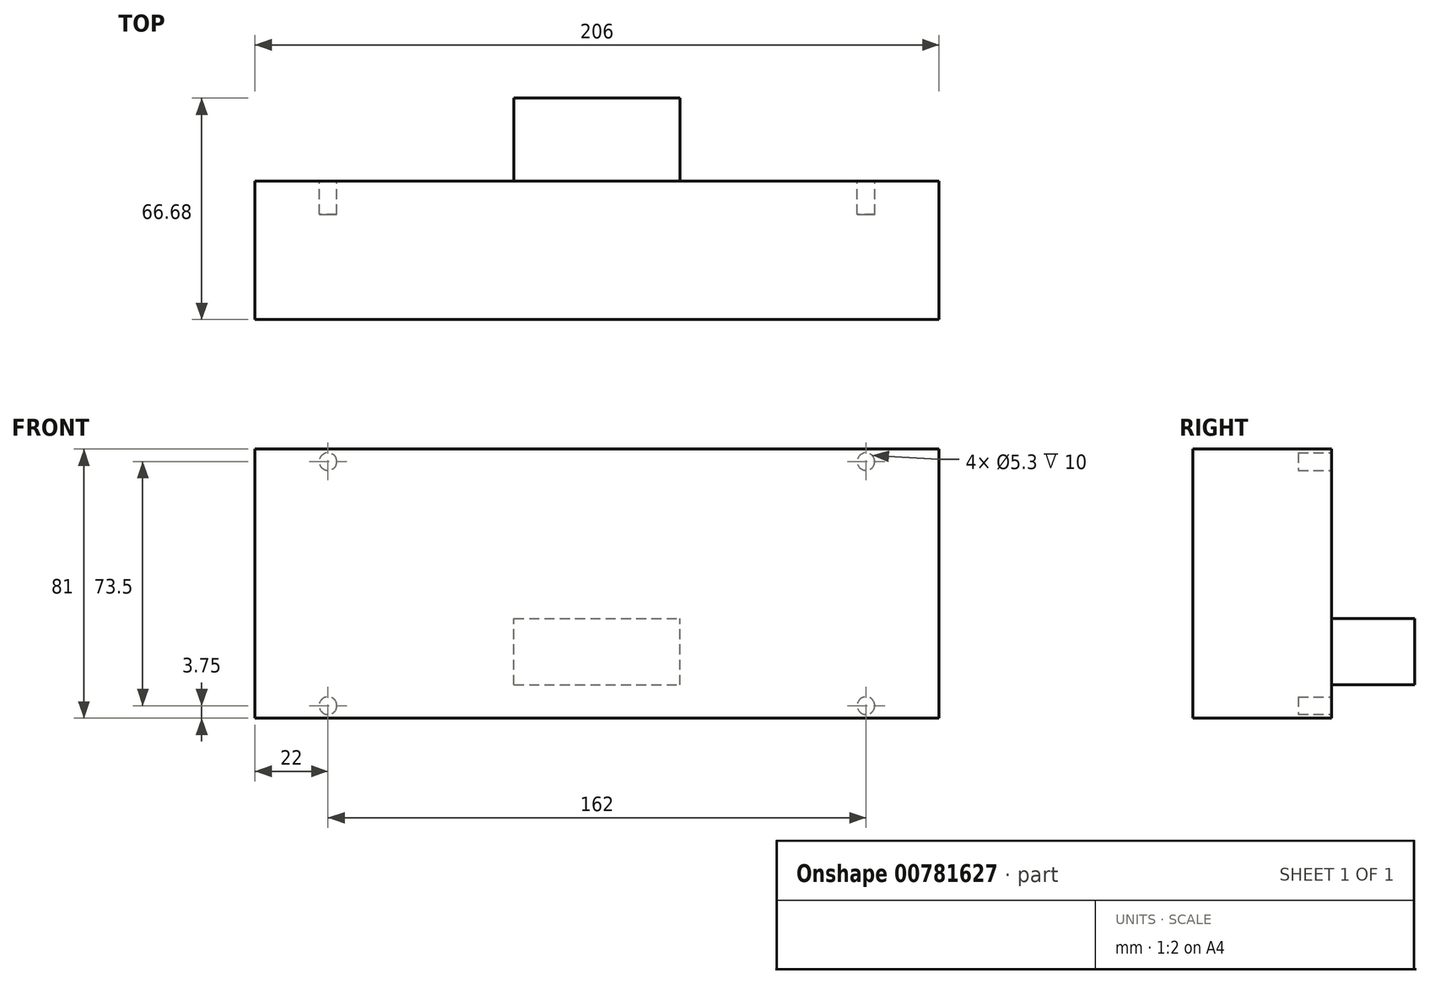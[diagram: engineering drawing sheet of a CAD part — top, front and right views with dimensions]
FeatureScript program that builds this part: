
annotation { "Feature Type Name" : "Feature", "Feature Type Description" : "" }
export const myFeature = defineFeature(function(context is Context, id is Id, definition is map)
    precondition{}
    {
        {
            var Q0;
            Q0=qCreatedBy(makeId("Front.planeOp"),FACE);
            var sketch = newSketch(context, id + "F0", { "sketchPlane" : qUnion([Q0])});
            skLineSegment(sketch, "E0.bottom", {"start": v(103, -40.5) * mm, "end": v(-103, -40.5) * mm});
            skLineSegment(sketch, "E0.top", {"start": v(103, 40.5) * mm, "end": v(-103, 40.5) * mm});
            skLineSegment(sketch, "E0.left", {"start": v(103, -40.5) * mm, "end": v(103, 40.5) * mm});
            skLineSegment(sketch, "E0.right", {"start": v(-103, -40.5) * mm, "end": v(-103, 40.5) * mm});
            skPoint(sketch, "E0.middle", {"position": v(0, 0) * mm});
            skSolve(sketch);
        }
        {
            var Q0;
            Q0 = qSketchRegion(id + "F0", true);
            extrude(context, id + "F1", {"entities" : qUnion([Q0]), "depth" : 41.68 * mm, "offsetDistance" : 25 * mm});
        }
        {
            var Q0;
            Q0=makeQuery(id+"F1.opExtrude","CAP_FACE",FACE,{"disambiguationData":[OSD([sQuery(id+"F0.wireOp",EDGE,"E0.bottom"),sQuery(id+"F0.wireOp",EDGE,"E0.top"),sQuery(id+"F0.wireOp",EDGE,"E0.left"),sQuery(id+"F0.wireOp",EDGE,"E0.right")])],"isStart":true});
            var sketch = newSketch(context, id + "F2", { "sketchPlane" : qUnion([Q0])});
            skLineSegment(sketch, "E1.bottom", {"start": v(81, -36.75) * mm, "end": v(-81, -36.75) * mm, "construction": true});
            skLineSegment(sketch, "E1.top", {"start": v(81, 36.75) * mm, "end": v(-81, 36.75) * mm, "construction": true});
            skLineSegment(sketch, "E1.left", {"start": v(81, -36.75) * mm, "end": v(81, 36.75) * mm, "construction": true});
            skLineSegment(sketch, "E1.right", {"start": v(-81, -36.75) * mm, "end": v(-81, 36.75) * mm, "construction": true});
            skPoint(sketch, "E1.middle", {"position": v(0, 0) * mm});
            skCircle(sketch, "E2", {"center": v(-81, 36.75) * mm, "radius": 2.65 * mm});
            skCircle(sketch, "E3", {"center": v(-81, -36.75) * mm, "radius": 2.65 * mm});
            skCircle(sketch, "E4", {"center": v(81, -36.75) * mm, "radius": 2.65 * mm});
            skCircle(sketch, "E5", {"center": v(81, 36.75) * mm, "radius": 2.65 * mm});
            skSolve(sketch);
        }
        {
            var Q0;
            Q0 = qSketchRegion(id + "F2", true);
            extrude(context, id + "F3", {"entities" : qUnion([Q0]), "operationType" : NewBodyOperationType.REMOVE, "oppositeDirection" : true, "depth" : 10 * mm, "offsetDistance" : 25 * mm});
        }
        {
            var Q0;
            Q0=makeQuery(id+"F1.opExtrude","CAP_FACE",FACE,{"disambiguationData":[OSD([sQuery(id+"F0.wireOp",EDGE,"E0.bottom"),sQuery(id+"F0.wireOp",EDGE,"E0.top"),sQuery(id+"F0.wireOp",EDGE,"E0.left"),sQuery(id+"F0.wireOp",EDGE,"E0.right")])],"isStart":true});
            var sketch = newSketch(context, id + "F4", { "sketchPlane" : qUnion([Q0])});
            skLineSegment(sketch, "E6.bottom", {"start": v(25, -30.5) * mm, "end": v(-25, -30.5) * mm});
            skLineSegment(sketch, "E6.top", {"start": v(25, -10.5) * mm, "end": v(-25, -10.5) * mm});
            skLineSegment(sketch, "E6.left", {"start": v(25, -30.5) * mm, "end": v(25, -10.5) * mm});
            skLineSegment(sketch, "E6.right", {"start": v(-25, -30.5) * mm, "end": v(-25, -10.5) * mm});
            skPoint(sketch, "E6.middle", {"position": v(0, -20.5) * mm});
            skSolve(sketch);
        }
        {
            var Q0;
            Q0 = qSketchRegion(id + "F4", true);
            extrude(context, id + "F5", {"entities" : qUnion([Q0]), "operationType" : NewBodyOperationType.ADD, "depth" : 25 * mm, "offsetDistance" : 25 * mm});
        }
    });
